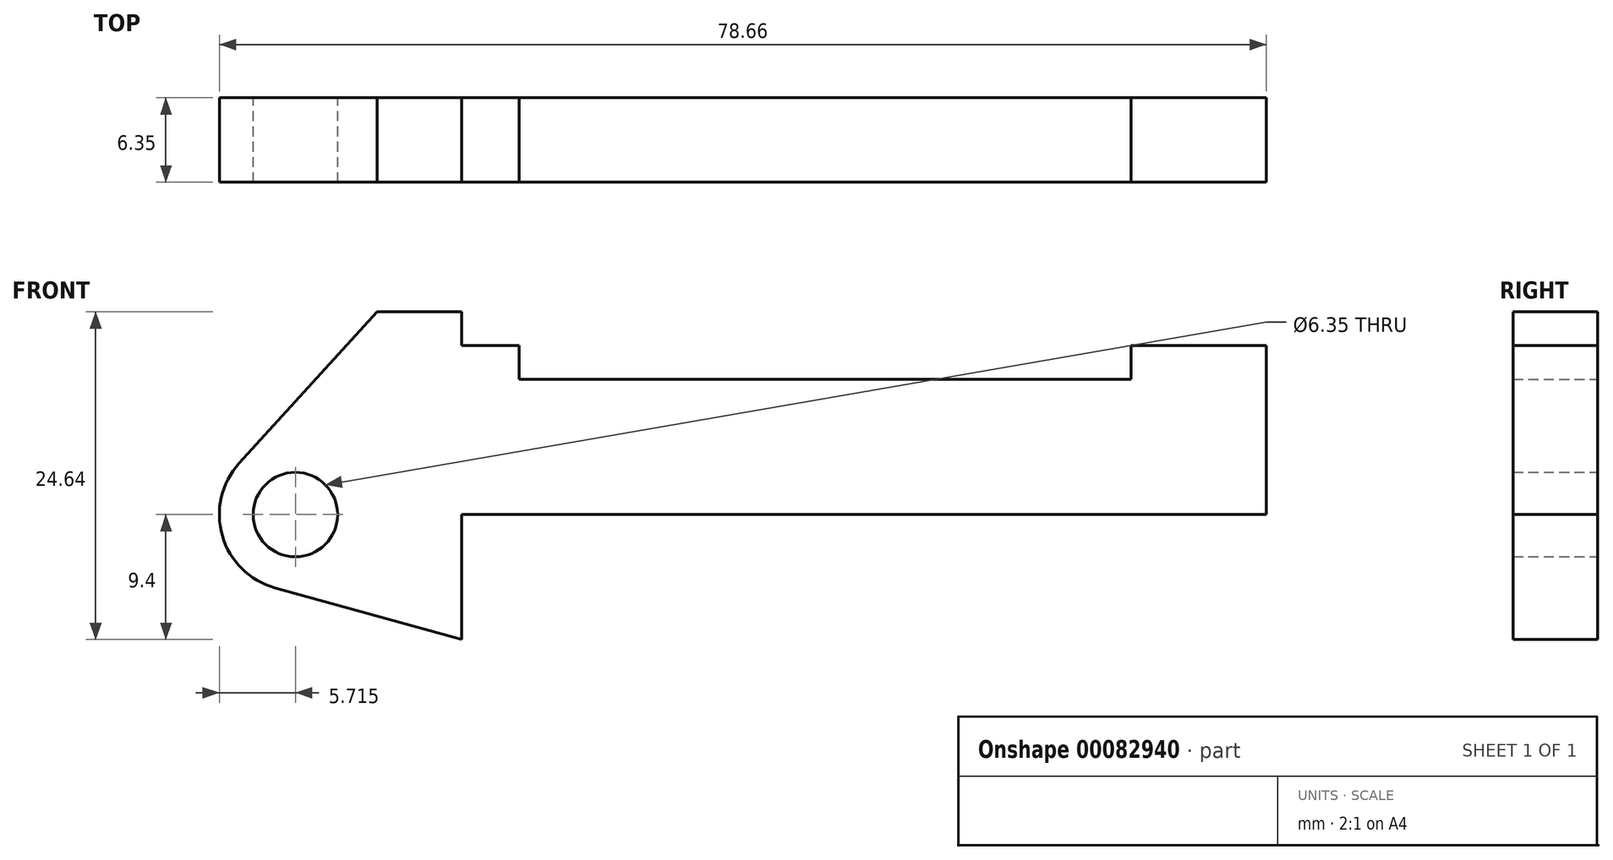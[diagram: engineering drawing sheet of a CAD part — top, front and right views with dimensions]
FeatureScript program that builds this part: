
annotation { "Feature Type Name" : "Feature", "Feature Type Description" : "" }
export const myFeature = defineFeature(function(context is Context, id is Id, definition is map)
    precondition{}
    {
        {
            var Q0;
            Q0=qCreatedBy(makeId("Front.planeOp"),FACE);
            var sketch = newSketch(context, id + "F0", { "sketchPlane" : qUnion([Q0])});
            skLineSegment(sketch, "E0", {"start": v(0, 0) * mm, "end": v(0, 12.7) * mm});
            skLineSegment(sketch, "E1", {"start": v(0, 12.7) * mm, "end": v(10.16, 12.7) * mm});
            skLineSegment(sketch, "E2", {"start": v(10.16, 12.7) * mm, "end": v(10.16, 10.16) * mm});
            skLineSegment(sketch, "E3", {"start": v(10.16, 10.16) * mm, "end": v(56.13, 10.16) * mm});
            skLineSegment(sketch, "E4", {"start": v(56.13, 10.16) * mm, "end": v(56.13, 12.7) * mm});
            skLineSegment(sketch, "E5", {"start": v(56.13, 12.7) * mm, "end": v(66.3, 12.7) * mm});
            skLineSegment(sketch, "E6", {"start": v(66.3, 12.7) * mm, "end": v(66.3, 0) * mm});
            skLineSegment(sketch, "E7", {"start": v(66.3, 0) * mm, "end": v(0, 0) * mm});
            skLineSegment(sketch, "E8", {"start": v(5.84, 15.24) * mm, "end": v(-0.5, 15.24) * mm});
            skLineSegment(sketch, "E9", {"start": v(-0.5, 15.24) * mm, "end": v(-10.88, 3.85) * mm});
            skLineSegment(sketch, "E10", {"start": v(0, 0) * mm, "end": v(-6.65, 0) * mm});
            skCircle(sketch, "E11", {"center": v(-6.65, 0) * mm, "radius": 5.72 * mm});
            skCircle(sketch, "E12", {"center": v(-6.65, 0) * mm, "radius": 3.18 * mm});
            skLineSegment(sketch, "E13", {"start": v(5.84, 15.24) * mm, "end": v(5.84, -9.4) * mm});
            skLineSegment(sketch, "E14", {"start": v(5.84, -9.4) * mm, "end": v(-8.18, -5.5) * mm});
            skSolve(sketch);
        }
        {
            var Q0;
            {var subQ3=sQuery(id+"F0.wireOp",EDGE,"E0");Q0=makeQuery(id+"F0.imprint","IMPRINT",FACE,{"disambiguationData":[TD([[makeQuery(id+"F0.imprint","IMPRINT",EDGE,{"derivedFrom":subQ3}),1.0]])]});}
            var Q1;
            {var subQ4=sQuery(id+"F0.wireOp",EDGE,"E12");Q1=makeQuery(id+"F0.imprint","IMPRINT",FACE,{"disambiguationData":[TD([[makeQuery(id+"F0.imprint","IMPRINT",EDGE,{"derivedFrom":subQ4}),-1.0]])]});}
            var Q2;
            {var subQ0=sQuery(id+"F0.wireOp",EDGE,"E14");Q2=makeQuery(id+"F0.imprint","IMPRINT",FACE,{"disambiguationData":[TD([[makeQuery(id+"F0.imprint","IMPRINT",EDGE,{"derivedFrom":subQ0}),-1.0]])]});}
            var Q3;
            {var subQ0=sQuery(id+"F0.wireOp",EDGE,"E0");Q3=makeQuery(id+"F0.imprint","IMPRINT",FACE,{"disambiguationData":[TD([[makeQuery(id+"F0.imprint","IMPRINT",EDGE,{"derivedFrom":subQ0}),-1.0]])]});}
            extrude(context, id + "F1", {"entities" : qUnion([Q0, Q1, Q2, Q3]), "depth" : 6.35 * mm});
        }
        {
            var Q0;
            {var subQ0=sQuery(id+"F0.wireOp",EDGE,"E2");Q0=makeQuery(id+"F0.imprint","IMPRINT",FACE,{"disambiguationData":[TD([[makeQuery(id+"F0.imprint","IMPRINT",EDGE,{"derivedFrom":subQ0}),-1.0]])]});}
            extrude(context, id + "F2", {"entities" : qUnion([Q0]), "operationType" : NewBodyOperationType.ADD, "depth" : 6.35 * mm});
        }
    });
